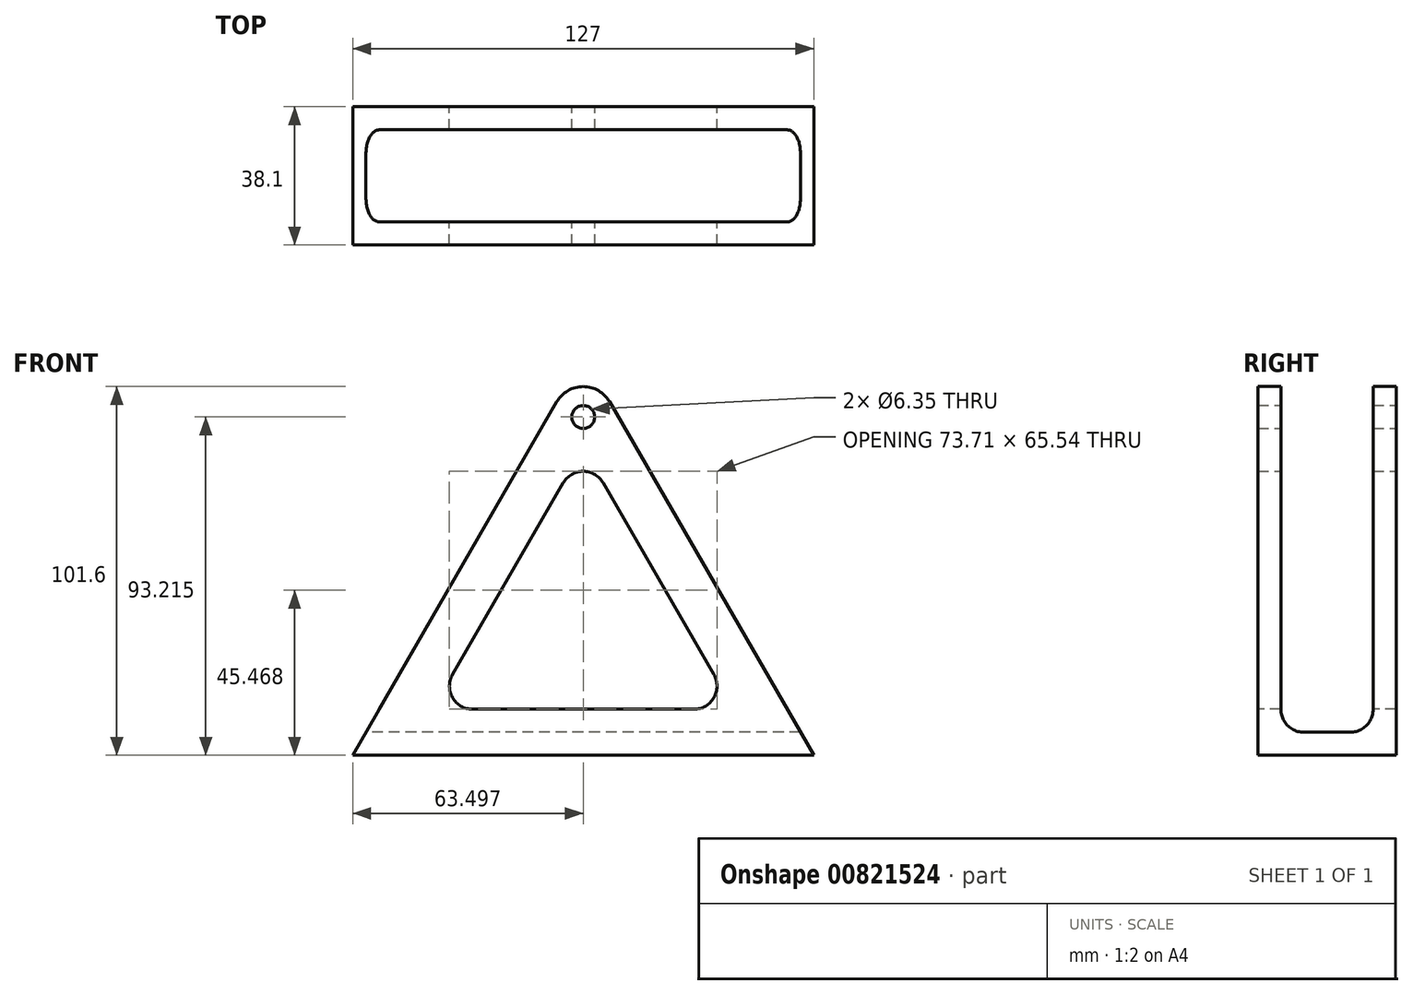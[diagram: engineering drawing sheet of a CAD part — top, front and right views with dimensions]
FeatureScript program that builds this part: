
annotation { "Feature Type Name" : "Feature", "Feature Type Description" : "" }
export const myFeature = defineFeature(function(context is Context, id is Id, definition is map)
    precondition{}
    {
        {
            var Q0;
            Q0=qCreatedBy(makeId("Front.planeOp"),FACE);
            var sketch = newSketch(context, id + "F0", { "sketchPlane" : qUnion([Q0])});
            skLineSegment(sketch, "E0", {"start": v(-105.81, -30.12) * mm, "end": v(21.19, -30.12) * mm});
            skLineSegment(sketch, "E1", {"start": v(21.19, -30.12) * mm, "end": v(-35.05, 67.29) * mm});
            skLineSegment(sketch, "E2", {"start": v(-105.81, -30.12) * mm, "end": v(-49.57, 67.29) * mm});
            skArc(sketch, "E3", {"start": v(-35.05, 67.29) * mm, "mid": v(-42.31, 71.48) * mm, "end": v(-49.57, 67.29) * mm});
            skCircle(sketch, "E4", {"center": v(-42.31, 63.1) * mm, "radius": 3.18 * mm});
            skSolve(sketch);
        }
        {
            var Q0;
            Q0=makeQuery(id+"F0.imprint","IMPRINT",FACE,{"disambiguationData":[TD([[makeQuery(id+"F0.imprint","IMPRINT",EDGE,{"derivedFrom":sQuery(id+"F0.wireOp",EDGE,"E0")}),1.0]])]});
            extrude(context, id + "F1", {"entities" : qUnion([Q0]), "depth" : 38.1 * mm, "offsetDistance" : 25.4 * mm});
        }
        {
            var Q0;
            Q0=makeQuery(id+"F1.opExtrude","SWEPT_FACE",FACE,{"disambiguationData":[OSD([sQuery(id+"F0.wireOp",EDGE,"E0")])]});
            cPlane(context, id + "F2", {"entities" : qUnion([Q0]), "cplaneType" : CPlaneType.OFFSET, "offset" : 6.35 * mm, "oppositeDirection" : true, "width" : 152.4 * mm, "height" : 152.4 * mm});
        }
        {
            var Q0;
            Q0=qCreatedBy(id+"F2.planeOp",FACE);
            var sketch = newSketch(context, id + "F3", { "sketchPlane" : qUnion([Q0])});
            skLineSegment(sketch, "E5.bottom", {"start": v(21.19, 31.75) * mm, "end": v(-105.81, 31.75) * mm});
            skLineSegment(sketch, "E5.top", {"start": v(21.19, 6.35) * mm, "end": v(-105.81, 6.35) * mm});
            skLineSegment(sketch, "E5.left", {"start": v(21.19, 31.75) * mm, "end": v(21.19, 6.35) * mm});
            skLineSegment(sketch, "E5.right", {"start": v(-105.81, 31.75) * mm, "end": v(-105.81, 6.35) * mm});
            skSolve(sketch);
        }
        {
            var Q0;
            Q0 = qSketchRegion(id + "F3", true);
            extrude(context, id + "F4", {"entities" : qUnion([Q0]), "operationType" : NewBodyOperationType.REMOVE, "endBound" : BoundingType.THROUGH_ALL, "oppositeDirection" : true, "depth" : 25.4 * mm, "offsetDistance" : 25.4 * mm});
        }
        {
            var Q0;
            Q0=makeQuery(id+"F1.opExtrude","CAP_FACE",FACE,{"disambiguationData":[OSD([sQuery(id+"F0.wireOp",EDGE,"E0"),sQuery(id+"F0.wireOp",EDGE,"E1"),sQuery(id+"F0.wireOp",EDGE,"E2"),sQuery(id+"F0.wireOp",EDGE,"E3"),sQuery(id+"F0.wireOp",EDGE,"E4")])],"isStart":false});
            var sketch = newSketch(context, id + "F5", { "sketchPlane" : qUnion([Q0])});
            skLineSegment(sketch, "E6", {"start": v(-42.31, 54.47) * mm, "end": v(-83.82, -17.42) * mm});
            skLineSegment(sketch, "E7", {"start": v(-83.82, -17.42) * mm, "end": v(-0.81, -17.42) * mm});
            skLineSegment(sketch, "E8", {"start": v(-0.81, -17.42) * mm, "end": v(-42.31, 54.47) * mm});
            skSolve(sketch);
        }
        {
            var Q0;
            Q0=makeQuery(id+"F5.imprint","IMPRINT",FACE,{"disambiguationData":[TD([[makeQuery(id+"F5.imprint","IMPRINT",EDGE,{"derivedFrom":sQuery(id+"F5.wireOp",EDGE,"E6")}),1.0]])]});
            extrude(context, id + "F6", {"entities" : qUnion([Q0]), "operationType" : NewBodyOperationType.REMOVE, "endBound" : BoundingType.THROUGH_ALL, "oppositeDirection" : true, "depth" : 25.4 * mm, "offsetDistance" : 25.4 * mm});
        }
        {
            var Q0;
            {var subQ0=sQuery(id+"F5.wireOp",EDGE,"E6");var subQ1=sQuery(id+"F5.wireOp",EDGE,"E8");Q0=makeQuery(id+"F6.boolean.opBoolean","COPY",EDGE,{"disambiguationData":[TD([makeQuery(id+"F4.boolean.opBoolean","COPY",FACE,{"derivedFrom":makeQuery(id+"F4.opExtrude","SWEPT_FACE",FACE,{"disambiguationData":[OSD([sQuery(id+"F3.wireOp",EDGE,"E5.bottom")])]})})])],"derivedFrom":makeQuery(id+"F6.opExtrude","SWEPT_EDGE",EDGE,{"disambiguationData":[OSD([subQ0,subQ1])]})});}
            var Q1;
            {var subQ0=sQuery(id+"F5.wireOp",EDGE,"E7");var subQ1=sQuery(id+"F5.wireOp",EDGE,"E6");Q1=makeQuery(id+"F6.boolean.opBoolean","COPY",EDGE,{"disambiguationData":[TD([makeQuery(id+"F4.boolean.opBoolean","COPY",FACE,{"derivedFrom":makeQuery(id+"F4.opExtrude","SWEPT_FACE",FACE,{"disambiguationData":[OSD([sQuery(id+"F3.wireOp",EDGE,"E5.bottom")])]})})])],"derivedFrom":makeQuery(id+"F6.opExtrude","SWEPT_EDGE",EDGE,{"disambiguationData":[OSD([subQ1,subQ0])]})});}
            var Q2;
            {var subQ0=sQuery(id+"F5.wireOp",EDGE,"E7");var subQ1=sQuery(id+"F5.wireOp",EDGE,"E8");Q2=makeQuery(id+"F6.boolean.opBoolean","COPY",EDGE,{"disambiguationData":[TD([makeQuery(id+"F4.boolean.opBoolean","COPY",FACE,{"derivedFrom":makeQuery(id+"F4.opExtrude","SWEPT_FACE",FACE,{"disambiguationData":[OSD([sQuery(id+"F3.wireOp",EDGE,"E5.bottom")])]})})])],"derivedFrom":makeQuery(id+"F6.opExtrude","SWEPT_EDGE",EDGE,{"disambiguationData":[OSD([subQ0,subQ1])]})});}
            var Q3;
            {var subQ0=sQuery(id+"F5.wireOp",EDGE,"E8");var subQ1=sQuery(id+"F5.wireOp",EDGE,"E7");Q3=makeQuery(id+"F6.boolean.opBoolean","COPY",EDGE,{"disambiguationData":[TD([makeQuery(id+"F4.boolean.opBoolean","COPY",FACE,{"derivedFrom":makeQuery(id+"F4.opExtrude","SWEPT_FACE",FACE,{"disambiguationData":[OSD([sQuery(id+"F3.wireOp",EDGE,"E5.top")])]})})])],"derivedFrom":makeQuery(id+"F6.opExtrude","SWEPT_EDGE",EDGE,{"disambiguationData":[OSD([subQ1,subQ0])]})});}
            var Q4;
            {var subQ0=sQuery(id+"F5.wireOp",EDGE,"E6");var subQ1=sQuery(id+"F5.wireOp",EDGE,"E7");Q4=makeQuery(id+"F6.boolean.opBoolean","COPY",EDGE,{"disambiguationData":[TD([makeQuery(id+"F4.boolean.opBoolean","COPY",FACE,{"derivedFrom":makeQuery(id+"F4.opExtrude","SWEPT_FACE",FACE,{"disambiguationData":[OSD([sQuery(id+"F3.wireOp",EDGE,"E5.top")])]})})])],"derivedFrom":makeQuery(id+"F6.opExtrude","SWEPT_EDGE",EDGE,{"disambiguationData":[OSD([subQ0,subQ1])]})});}
            var Q5;
            {var subQ0=sQuery(id+"F5.wireOp",EDGE,"E8");var subQ1=sQuery(id+"F5.wireOp",EDGE,"E6");Q5=makeQuery(id+"F6.boolean.opBoolean","COPY",EDGE,{"disambiguationData":[TD([makeQuery(id+"F4.boolean.opBoolean","COPY",FACE,{"derivedFrom":makeQuery(id+"F4.opExtrude","SWEPT_FACE",FACE,{"disambiguationData":[OSD([sQuery(id+"F3.wireOp",EDGE,"E5.top")])]})})])],"derivedFrom":makeQuery(id+"F6.opExtrude","SWEPT_EDGE",EDGE,{"disambiguationData":[OSD([subQ1,subQ0])]})});}
            fillet(context, id + "F7", {"entities" : qUnion([Q0, Q1, Q2, Q3, Q4, Q5]), "radius" : 6.35 * mm, "tangentPropagation" : true, "allowEdgeOverflow" : false});
        }
        {
            var Q0;
            Q0=makeQuery(id+"F4.boolean.opBoolean","COPY",EDGE,{"derivedFrom":makeQuery(id+"F4.opExtrude","CAP_EDGE",EDGE,{"disambiguationData":[OSD([sQuery(id+"F3.wireOp",EDGE,"E5.top")])],"isStart":true})});
            var Q1;
            Q1=makeQuery(id+"F4.boolean.opBoolean","COPY",EDGE,{"derivedFrom":makeQuery(id+"F4.opExtrude","CAP_EDGE",EDGE,{"disambiguationData":[OSD([sQuery(id+"F3.wireOp",EDGE,"E5.bottom")])],"isStart":true})});
            fillet(context, id + "F8", {"entities" : qUnion([Q0, Q1]), "radius" : 6.35 * mm, "tangentPropagation" : true, "allowEdgeOverflow" : false});
        }
    });
